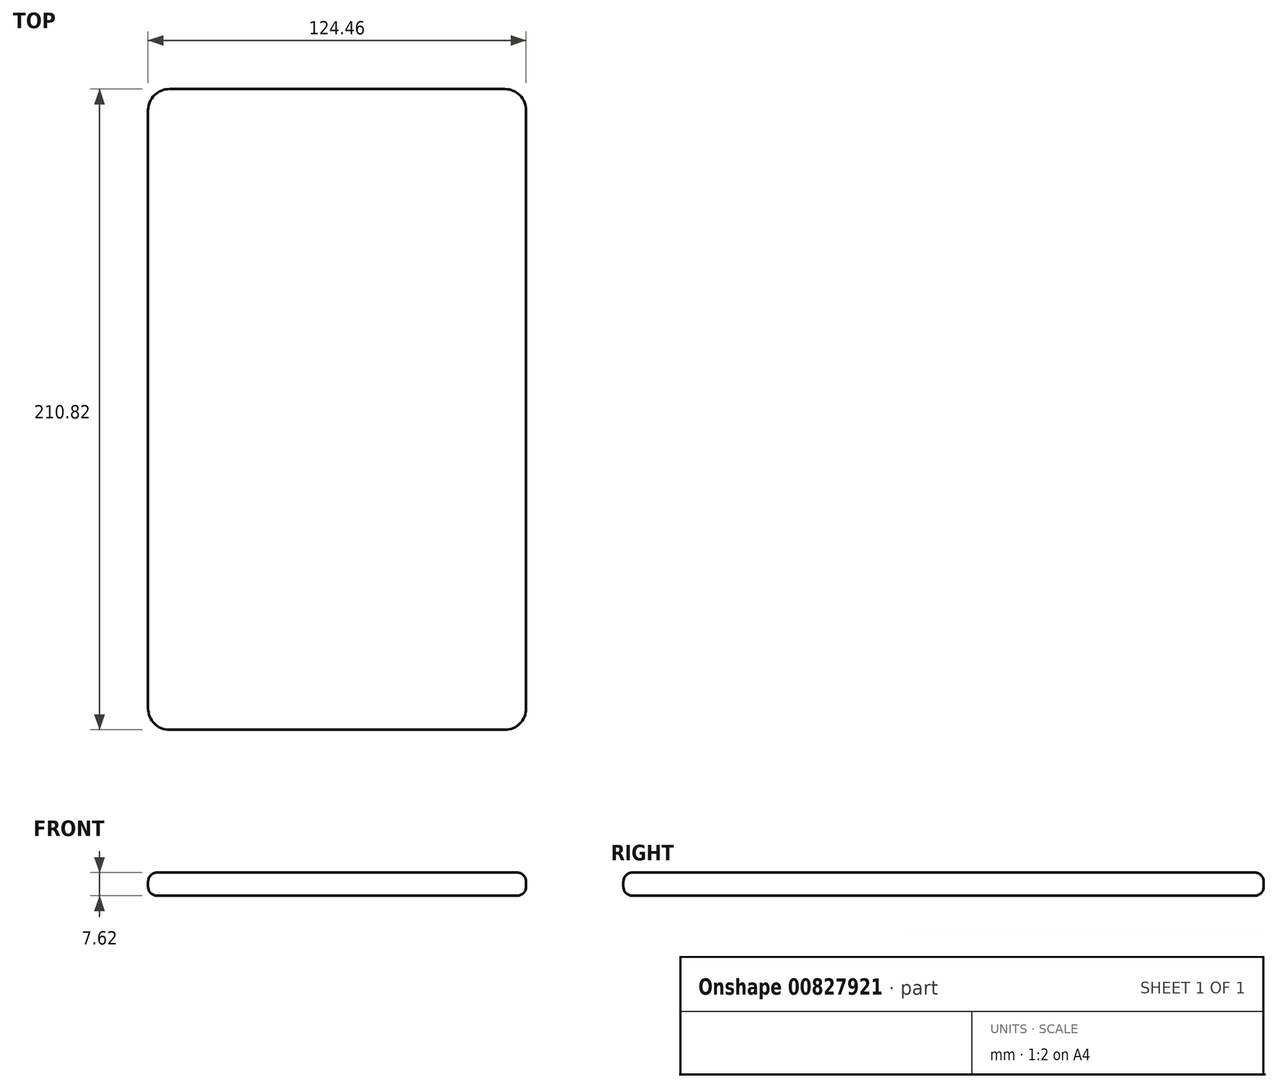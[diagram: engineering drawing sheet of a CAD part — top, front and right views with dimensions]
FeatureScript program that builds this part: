
annotation { "Feature Type Name" : "Feature", "Feature Type Description" : "" }
export const myFeature = defineFeature(function(context is Context, id is Id, definition is map)
    precondition{}
    {
        {
            var Q0;
            Q0=qCreatedBy(makeId("Top.planeOp"),FACE);
            var sketch = newSketch(context, id + "F0", { "sketchPlane" : qUnion([Q0])});
            skLineSegment(sketch, "E0.bottom", {"start": v(-55.23, -105.4) * mm, "end": v(55.23, -105.4) * mm});
            skLineSegment(sketch, "E0.top", {"start": v(-55.23, 105.41) * mm, "end": v(55.23, 105.41) * mm});
            skLineSegment(sketch, "E0.left", {"start": v(-62.23, -98.4) * mm, "end": v(-62.23, 98.41) * mm});
            skLineSegment(sketch, "E0.right", {"start": v(62.23, -98.41) * mm, "end": v(62.23, 98.41) * mm});
            skPoint(sketch, "E1.visualSharp", {"position": v(-62.23, 105.41) * mm});
            skArc(sketch, "E1.filletArc", {"start": v(-55.23, 105.41) * mm, "mid": v(-60.18, 103.36) * mm, "end": v(-62.23, 98.41) * mm});
            skPoint(sketch, "E2.visualSharp", {"position": v(62.23, 105.41) * mm});
            skArc(sketch, "E2.filletArc", {"start": v(62.23, 98.41) * mm, "mid": v(60.18, 103.36) * mm, "end": v(55.23, 105.41) * mm});
            skPoint(sketch, "E3.visualSharp", {"position": v(62.23, -105.4) * mm});
            skArc(sketch, "E3.filletArc", {"start": v(55.23, -105.41) * mm, "mid": v(60.18, -103.36) * mm, "end": v(62.23, -98.41) * mm});
            skPoint(sketch, "E4.visualSharp", {"position": v(-62.23, -105.4) * mm});
            skArc(sketch, "E4.filletArc", {"start": v(-62.23, -98.4) * mm, "mid": v(-60.18, -103.36) * mm, "end": v(-55.23, -105.4) * mm});
            skPoint(sketch, "E5", {"position": v(0, 105.41) * mm});
            skPoint(sketch, "E6", {"position": v(62.23, 0) * mm});
            skPoint(sketch, "E6.positionSnap0", {"position": v(62.23, 0) * mm});
            skSolve(sketch);
        }
        {
            var Q0;
            Q0 = qSketchRegion(id + "F0", true);
            extrude(context, id + "F1", {"entities" : qUnion([Q0]), "depth" : 7.62 * mm, "offsetDistance" : 25 * mm});
        }
        {
            var Q0;
            Q0=makeQuery(id+"F1.opExtrude","CAP_EDGE",EDGE,{"disambiguationData":[OSD([sQuery(id+"F0.wireOp",EDGE,"E0.left")])],"isStart":false});
            fillet(context, id + "F2", {"entities" : qUnion([Q0]), "radius" : 3 * mm, "tangentPropagation" : true, "allowEdgeOverflow" : false});
        }
        {
            var Q0;
            Q0=makeQuery(id+"F1.opExtrude","CAP_FACE",FACE,{"disambiguationData":[OSD([sQuery(id+"F0.wireOp",EDGE,"E0.bottom"),sQuery(id+"F0.wireOp",EDGE,"E0.top"),sQuery(id+"F0.wireOp",EDGE,"E0.left"),sQuery(id+"F0.wireOp",EDGE,"E0.right"),sQuery(id+"F0.wireOp",EDGE,"E1.filletArc"),sQuery(id+"F0.wireOp",EDGE,"E2.filletArc"),sQuery(id+"F0.wireOp",EDGE,"E3.filletArc"),sQuery(id+"F0.wireOp",EDGE,"E4.filletArc")])],"isStart":true});
            fillet(context, id + "F3", {"entities" : qUnion([Q0]), "radius" : 3 * mm, "tangentPropagation" : true, "allowEdgeOverflow" : false});
        }
    });
